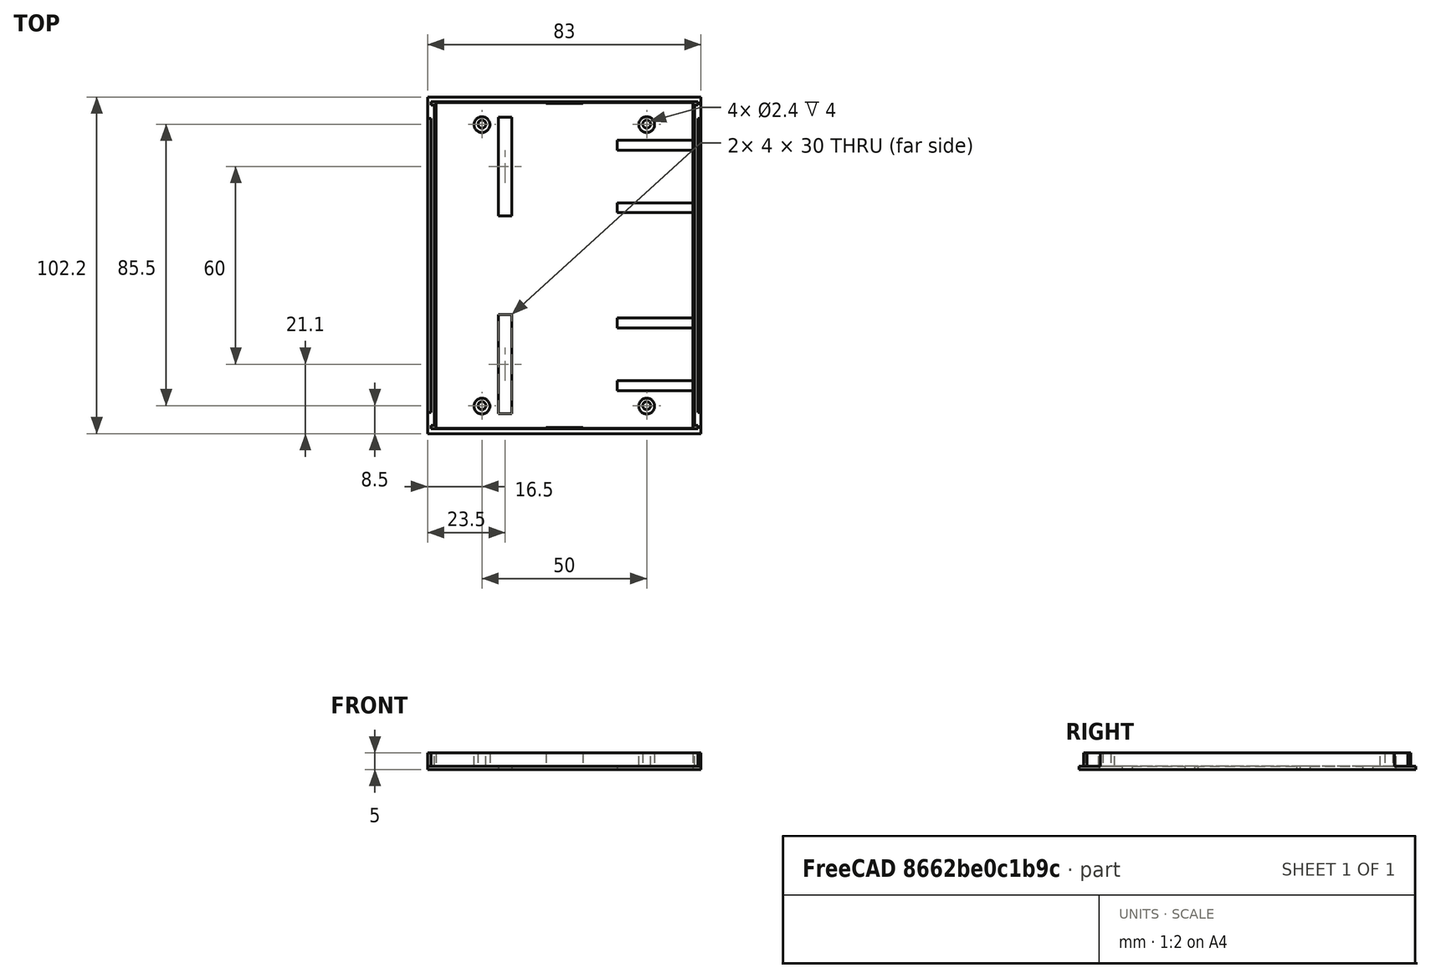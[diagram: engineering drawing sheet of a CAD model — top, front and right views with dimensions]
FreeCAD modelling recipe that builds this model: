
FCSTD DOCUMENT  (FreeCAD 1.0R39109 (Git))
Label: parte de abajo 2.0
License: All rights reserved
LicenseURL: https://en.wikipedia.org/wiki/All_rights_reserved
objects: Sketcher::SketchObject×4, PartDesign::Pad×2, PartDesign::Pocket×2, PartDesign::Body×1
note: 21 computed .brp shape members not serialized (recipe doc carries the construction recipe); baked Part::Feature solids carry a one-line shape summary decoded from their .brp

FEATURE [Sketcher::SketchObject] Sketch
  ArcFitTolerance = 1e-06
  AttachmentSupport = -> [XY_Plane]
  FullyConstrained = true
  MakeInternals = false
  MapMode = 5
  sketch-geometry (5):
    g0: LineSegment StartX=-41.5 StartY=-51.1 StartZ=0 EndX=41.5 EndY=-51.1 EndZ=0
    g1: LineSegment StartX=41.5 StartY=-51.1 StartZ=0 EndX=41.5 EndY=51.1 EndZ=0
    g2: LineSegment StartX=41.5 StartY=51.1 StartZ=0 EndX=-41.5 EndY=51.1 EndZ=0
    g3: LineSegment StartX=-41.5 StartY=51.1 StartZ=0 EndX=-41.5 EndY=-51.1 EndZ=0
    g4: GeomPoint [constr] X=0 Y=0 Z=0
  constraints (12):
    c: Coincident(g0,g1)
    c: Coincident(g1,g2)
    c: Coincident(g2,g3)
    c: Coincident(g3,g0)
    c: Horizontal(g0)
    c: Horizontal(g2)
    c: Vertical(g1)
    c: Vertical(g3)
    c: Symmetric(g2,g0,g4)
    c: Coincident(g4,g-1)
    c: DistanceX(g2,g2) = 83
    c: DistanceY(g1,g1) = 102.2
FEATURE [PartDesign::Pad] Pad
  Direction = (0,0,1)
  Length = 1
  Length2 = 10
  Profile = -> Sketch
  ReferenceAxis = -> Sketch [N_Axis]
  Refine = true
  Suppressed = false
  Type = 0
FEATURE [Sketcher::SketchObject] Sketch001
  ArcFitTolerance = 1e-06
  AttachmentSupport = -> [Pad]
  ExternalGeometry = -> [Pad]
  FullyConstrained = true
  MakeInternals = false
  MapMode = 5
  Placement = pos=(0,0,1) rot=(0,0,1;0rad)
  sketch-geometry (33):
    g0: LineSegment StartX=-39.5 StartY=-49.65 StartZ=0 EndX=39.5 EndY=-49.65 EndZ=0
    g1: LineSegment StartX=39.5 StartY=-49.65 StartZ=0 EndX=39.5 EndY=49.65 EndZ=0
    g2: LineSegment StartX=39.5 StartY=49.65 StartZ=0 EndX=-39.5 EndY=49.65 EndZ=0
    g3: LineSegment StartX=-39.5 StartY=49.65 StartZ=0 EndX=-39.5 EndY=-49.65 EndZ=0
    g4: GeomPoint [constr] X=0 Y=0 Z=0
    g5: LineSegment StartX=41.5 StartY=44.65 StartZ=0 EndX=40.5 EndY=44.65 EndZ=0
    g6: LineSegment StartX=40.5 StartY=44.65 StartZ=0 EndX=40.5 EndY=-44.65 EndZ=0
    g7: LineSegment StartX=40.5 StartY=-44.65 StartZ=0 EndX=41.5 EndY=-44.65 EndZ=0
    g8: LineSegment StartX=41.5 StartY=-44.65 StartZ=0 EndX=41.5 EndY=44.65 EndZ=0
    g9: LineSegment StartX=-41.5 StartY=44.65 StartZ=0 EndX=-41.5 EndY=-44.65 EndZ=0
    g10: LineSegment StartX=-41.5 StartY=-44.65 StartZ=0 EndX=-40.5 EndY=-44.65 EndZ=0
    g11: LineSegment StartX=-40.5 StartY=-44.65 StartZ=0 EndX=-40.5 EndY=44.65 EndZ=0
    g12: LineSegment StartX=-40.5 StartY=44.65 StartZ=0 EndX=-41.5 EndY=44.65 EndZ=0
    g13: LineSegment StartX=39.5 StartY=-49.65 StartZ=0 EndX=40.5 EndY=-49.65 EndZ=0
    g14: LineSegment StartX=40.5 StartY=-49.65 StartZ=0 EndX=40.5 EndY=-48.65 EndZ=0
    g15: LineSegment StartX=40.5 StartY=-48.65 StartZ=0 EndX=39.5 EndY=-48.65 EndZ=0
    g16: LineSegment StartX=39.5 StartY=-48.65 StartZ=0 EndX=39.5 EndY=-49.65 EndZ=0
    g17: LineSegment StartX=-39.5 StartY=-49.65 StartZ=0 EndX=-39.5 EndY=-48.65 EndZ=0
    g18: LineSegment StartX=-39.5 StartY=-48.65 StartZ=0 EndX=-40.5 EndY=-48.65 EndZ=0
    g19: LineSegment StartX=-40.5 StartY=-48.65 StartZ=0 EndX=-40.5 EndY=-49.65 EndZ=0
    g20: LineSegment StartX=-40.5 StartY=-49.65 StartZ=0 EndX=-39.5 EndY=-49.65 EndZ=0
    g21: LineSegment StartX=-39.5 StartY=49.65 StartZ=0 EndX=-40.5 EndY=49.65 EndZ=0
    g22: LineSegment StartX=-40.5 StartY=49.65 StartZ=0 EndX=-40.5 EndY=48.65 EndZ=0
    g23: LineSegment StartX=-40.5 StartY=48.65 StartZ=0 EndX=-39.5 EndY=48.65 EndZ=0
    g24: LineSegment StartX=-39.5 StartY=48.65 StartZ=0 EndX=-39.5 EndY=49.65 EndZ=0
    g25: LineSegment StartX=39.5 StartY=49.65 StartZ=0 EndX=39.5 EndY=48.65 EndZ=0
    g26: LineSegment StartX=39.5 StartY=48.65 StartZ=0 EndX=40.5 EndY=48.65 EndZ=0
    g27: LineSegment StartX=40.5 StartY=48.65 StartZ=0 EndX=40.5 EndY=49.65 EndZ=0
    g28: LineSegment StartX=40.5 StartY=49.65 StartZ=0 EndX=39.5 EndY=49.65 EndZ=0
    g29: Circle CenterX=-25 CenterY=42.9 CenterZ=0 NormalX=0 NormalY=0 NormalZ=1 AngleXU=0 Radius=1.2
    g30: Circle CenterX=25 CenterY=42.9 CenterZ=0 NormalX=0 NormalY=0 NormalZ=1 AngleXU=0 Radius=1.2
    g31: Circle CenterX=-25 CenterY=-42.6 CenterZ=0 NormalX=0 NormalY=0 NormalZ=1 AngleXU=0 Radius=1.2
    g32: Circle CenterX=25 CenterY=-42.6 CenterZ=0 NormalX=0 NormalY=0 NormalZ=1 AngleXU=0 Radius=1.2
  constraints (92):
    c: Coincident(g0,g1)
    c: Coincident(g1,g2)
    c: Coincident(g2,g3)
    c: Coincident(g3,g0)
    c: Horizontal(g0)
    c: Horizontal(g2)
    c: Vertical(g1)
    c: Vertical(g3)
    c: Symmetric(g2,g0,g4)
    c: Coincident(g4,g-1)
    c: DistanceY(g1,g1) = 99.3
    c: DistanceX(g2,g2) = 79
    c: Coincident(g5,g6)
    c: Coincident(g6,g7)
    c: Coincident(g7,g8)
    c: Coincident(g8,g5)
    c: Horizontal(g5)
    c: Horizontal(g7)
    c: Vertical(g6)
    c: Vertical(g8)
    c: PointOnObject(g5,g-6)
    c: DistanceX(g5,g5) = 1
    c: DistanceY(g8,g8) = 89.3
    c: DistanceY(g0,g7) = 5
    c: Coincident(g9,g10)
    c: Coincident(g10,g11)
    c: Coincident(g11,g12)
    c: Coincident(g12,g9)
    c: Vertical(g9)
    c: Vertical(g11)
    c: Horizontal(g10)
    c: Horizontal(g12)
    c: PointOnObject(g9,g-4)
    c: DistanceX(g12,g12) = 1
    c: DistanceY(g9,g9) = 89.3
    c: Distance(g0,g10) = 5
    c: Coincident(g13,g14)
    c: Coincident(g14,g15)
    c: Coincident(g15,g16)
    c: Coincident(g16,g13)
    c: Horizontal(g13)
    c: Horizontal(g15)
    c: Vertical(g14)
    c: Vertical(g16)
    c: Coincident(g13,g0)
    c: DistanceX(g15,g15) = 1
    c: DistanceY(g14,g14) = 1
    c: Coincident(g17,g18)
    c: Coincident(g18,g19)
    c: Coincident(g19,g20)
    c: Coincident(g20,g17)
    c: Vertical(g17)
    c: Vertical(g19)
    c: Horizontal(g18)
    c: Horizontal(g20)
    c: Coincident(g17,g0)
    c: DistanceX(g18,g18) = 1
    c: DistanceY(g19,g19) = 1
    c: Coincident(g21,g22)
    c: Coincident(g22,g23)
    c: Coincident(g23,g24)
    c: Coincident(g24,g21)
    c: Horizontal(g21)
    c: Horizontal(g23)
    c: Vertical(g22)
    c: Vertical(g24)
    c: Coincident(g21,g2)
    c: DistanceY(g22,g22) = 1
    c: DistanceX(g23,g23) = 1
    c: Coincident(g25,g26)
    c: Coincident(g26,g27)
    c: Coincident(g27,g28)
    c: Coincident(g28,g25)
    c: Vertical(g25)
    c: Vertical(g27)
    c: Horizontal(g26)
    c: Horizontal(g28)
    c: Coincident(g25,g1)
    c: DistanceX(g26,g26) = 1
    c: DistanceY(g27,g27) = 1
    c: Diameter(g29) = 2.4
    c: Distance(g29,g2) = 6.75
    c: Diameter(g30) = 2.4
    c: Distance(g30,g2) = 6.75
    c: DistanceX(g29,g30) = 50
    c: Distance(g29,g3) = 14.5
    c: Diameter(g31) = 2.4
    c: Distance(g29,g31) = 85.5
    c: Distance(g31,g3) = 14.5
    c: DistanceX(g31,g32) = 50
    c: Diameter(g32) = 2.4
    c: DistanceY(g32,g30) = 85.5
FEATURE [PartDesign::Pad] Pad001
  BaseFeature = -> Pad
  Direction = (0,0,1)
  Length = 4
  Length2 = 10
  Profile = -> Sketch001
  ReferenceAxis = -> Sketch001 [N_Axis]
  Refine = true
  Suppressed = false
  Type = 0
FEATURE [Sketcher::SketchObject] Sketch002
  ArcFitTolerance = 1e-06
  AttachmentSupport = -> [Pad001]
  ExternalGeometry = -> [Pad001]
  FullyConstrained = true
  MakeInternals = false
  MapMode = 5
  Placement = pos=(0,0,5) rot=(0,0,1;0rad)
  sketch-geometry (17):
    g0: LineSegment StartX=-39 StartY=-49.5 StartZ=0 EndX=39 EndY=-49.5 EndZ=0
    g1: LineSegment StartX=39 StartY=-49.5 StartZ=0 EndX=39 EndY=49.5 EndZ=0
    g2: LineSegment StartX=39 StartY=49.5 StartZ=0 EndX=-39 EndY=49.5 EndZ=0
    g3: LineSegment StartX=-39 StartY=49.5 StartZ=0 EndX=-39 EndY=-49.5 EndZ=0
    g4: GeomPoint [constr] X=0 Y=0 Z=0
    g5: LineSegment StartX=-5.6 StartY=-49.5 StartZ=0 EndX=5.6 EndY=-49.5 EndZ=0
    g6: LineSegment StartX=5.6 StartY=-49.5 StartZ=0 EndX=5.6 EndY=-49.2 EndZ=0
    g7: LineSegment StartX=5.6 StartY=-49.2 StartZ=0 EndX=-5.6 EndY=-49.2 EndZ=0
    g8: LineSegment StartX=-5.6 StartY=-49.2 StartZ=0 EndX=-5.6 EndY=-49.5 EndZ=0
    g9: Circle CenterX=-25 CenterY=-42.75 CenterZ=0 NormalX=0 NormalY=0 NormalZ=1 AngleXU=0 Radius=2.4
    g10: Circle CenterX=-25 CenterY=42.75 CenterZ=0 NormalX=0 NormalY=0 NormalZ=1 AngleXU=0 Radius=2.4
    g11: Circle CenterX=25 CenterY=42.75 CenterZ=0 NormalX=0 NormalY=0 NormalZ=1 AngleXU=0 Radius=2.4
    g12: Circle CenterX=25 CenterY=-42.75 CenterZ=0 NormalX=0 NormalY=0 NormalZ=1 AngleXU=0 Radius=2.4
    g13: LineSegment StartX=-5.6 StartY=49.5 StartZ=0 EndX=-5.6 EndY=49.2 EndZ=0
    g14: LineSegment StartX=-5.6 StartY=49.2 StartZ=0 EndX=5.6 EndY=49.2 EndZ=0
    g15: LineSegment StartX=5.6 StartY=49.2 StartZ=0 EndX=5.6 EndY=49.5 EndZ=0
    g16: LineSegment StartX=5.6 StartY=49.5 StartZ=0 EndX=-5.6 EndY=49.5 EndZ=0
  constraints (48):
    c: Coincident(g0,g1)
    c: Coincident(g1,g2)
    c: Coincident(g2,g3)
    c: Coincident(g3,g0)
    c: Horizontal(g0)
    c: Horizontal(g2)
    c: Vertical(g1)
    c: Vertical(g3)
    c: Symmetric(g2,g0,g4)
    c: Coincident(g4,g-1)
    c: DistanceX(g2,g2) = 78
    c: DistanceY(g1,g1) = 99
    c: Coincident(g5,g6)
    c: Coincident(g6,g7)
    c: Coincident(g7,g8)
    c: Coincident(g8,g5)
    c: Horizontal(g5)
    c: Horizontal(g7)
    c: Vertical(g6)
    c: Vertical(g8)
    c: PointOnObject(g5,g0)
    c: DistanceX(g7,g7) = 11.2
    c: DistanceY(g6,g6) = 0.3
    c: Distance(g0,g8) = 33.4
    c: Diameter(g9) = 4.8
    c: Distance(g9,g3) = 14
    c: Diameter(g10) = 4.8
    c: Distance(g10,g2) = 6.75
    c: Distance(g10,g3) = 14
    c: DistanceY(g9,g10) = 85.5
    c: Diameter(g11) = 4.8
    c: Distance(g11,g2) = 6.75
    c: Distance(g10,g11) = 50
    c: Diameter(g12) = 4.8
    c: DistanceX(g9,g12) = 50
    c: DistanceY(g12,g11) = 85.5
    c: Coincident(g13,g14)
    c: Coincident(g14,g15)
    c: Coincident(g15,g16)
    c: Coincident(g16,g13)
    c: Vertical(g13)
    c: Vertical(g15)
    c: Horizontal(g14)
    c: Horizontal(g16)
    c: PointOnObject(g13,g2)
    c: DistanceY(g13,g13) = 0.3
    c: DistanceX(g14,g14) = 11.2
    c: Distance(g1,g15) = 33.4
FEATURE [PartDesign::Pocket] Pocket
  BaseFeature = -> Pad001
  Direction = (0,0,-1)
  Length = 4
  Length2 = 5
  Profile = -> Sketch002
  ReferenceAxis = -> Sketch002 [N_Axis]
  Refine = true
  Suppressed = false
  Type = 0
FEATURE [Sketcher::SketchObject] Sketch003
  ArcFitTolerance = 1e-06
  AttachmentSupport = -> [Pocket]
  ExternalGeometry = -> [Pocket]
  FullyConstrained = true
  MakeInternals = false
  MapMode = 5
  Placement = pos=(0,0,1) rot=(0,0,1;0rad)
  sketch-geometry (24):
    g0: LineSegment StartX=-20 StartY=-15 StartZ=0 EndX=-20 EndY=-45 EndZ=0
    g1: LineSegment StartX=-20 StartY=-45 StartZ=0 EndX=-16 EndY=-45 EndZ=0
    g2: LineSegment StartX=-16 StartY=-45 StartZ=0 EndX=-16 EndY=-15 EndZ=0
    g3: LineSegment StartX=-16 StartY=-15 StartZ=0 EndX=-20 EndY=-15 EndZ=0
    g4: LineSegment StartX=-20 StartY=45 StartZ=0 EndX=-20 EndY=15 EndZ=0
    g5: LineSegment StartX=-20 StartY=15 StartZ=0 EndX=-16 EndY=15 EndZ=0
    g6: LineSegment StartX=-16 StartY=15 StartZ=0 EndX=-16 EndY=45 EndZ=0
    g7: LineSegment StartX=-16 StartY=45 StartZ=0 EndX=-20 EndY=45 EndZ=0
    g8: LineSegment StartX=16 StartY=38 StartZ=0 EndX=16 EndY=35 EndZ=0
    g9: LineSegment StartX=16 StartY=35 StartZ=0 EndX=39 EndY=35 EndZ=0
    g10: LineSegment StartX=39 StartY=35 StartZ=0 EndX=39 EndY=38 EndZ=0
    g11: LineSegment StartX=39 StartY=38 StartZ=0 EndX=16 EndY=38 EndZ=0
    g12: LineSegment StartX=16 StartY=19 StartZ=0 EndX=16 EndY=16 EndZ=0
    g13: LineSegment StartX=16 StartY=16 StartZ=0 EndX=39 EndY=16 EndZ=0
    g14: LineSegment StartX=39 StartY=16 StartZ=0 EndX=39 EndY=19 EndZ=0
    g15: LineSegment StartX=39 StartY=19 StartZ=0 EndX=16 EndY=19 EndZ=0
    g16: LineSegment StartX=16 StartY=-16 StartZ=0 EndX=16 EndY=-19 EndZ=0
    g17: LineSegment StartX=16 StartY=-19 StartZ=0 EndX=39 EndY=-19 EndZ=0
    g18: LineSegment StartX=39 StartY=-19 StartZ=0 EndX=39 EndY=-16 EndZ=0
    g19: LineSegment StartX=39 StartY=-16 StartZ=0 EndX=16 EndY=-16 EndZ=0
    g20: LineSegment StartX=16 StartY=-35 StartZ=0 EndX=16 EndY=-38 EndZ=0
    g21: LineSegment StartX=16 StartY=-38 StartZ=0 EndX=39 EndY=-38 EndZ=0
    g22: LineSegment StartX=39 StartY=-38 StartZ=0 EndX=39 EndY=-35 EndZ=0
    g23: LineSegment StartX=39 StartY=-35 StartZ=0 EndX=16 EndY=-35 EndZ=0
  constraints (72):
    c: Coincident(g0,g1)
    c: Coincident(g1,g2)
    c: Coincident(g2,g3)
    c: Coincident(g3,g0)
    c: Vertical(g0)
    c: Vertical(g2)
    c: Horizontal(g1)
    c: Horizontal(g3)
    c: Coincident(g4,g5)
    c: Coincident(g5,g6)
    c: Coincident(g6,g7)
    c: Coincident(g7,g4)
    c: Vertical(g4)
    c: Vertical(g6)
    c: Horizontal(g5)
    c: Horizontal(g7)
    c: DistanceY(g6,g6) = 30
    c: DistanceX(g5,g5) = 4
    c: DistanceX(g3,g3) = 4
    c: DistanceY(g2,g2) = 30
    c: Distance(g-1,g3) = 15
    c: Distance(g-2,g2) = 16
    c: Distance(g-2,g6) = 16
    c: Distance(g-1,g5) = 15
    c: Coincident(g8,g9)
    c: Coincident(g9,g10)
    c: Coincident(g10,g11)
    c: Coincident(g11,g8)
    c: Vertical(g8)
    c: Vertical(g10)
    c: Horizontal(g9)
    c: Horizontal(g11)
    c: Coincident(g12,g13)
    c: Coincident(g13,g14)
    c: Coincident(g14,g15)
    c: Coincident(g15,g12)
    c: Vertical(g12)
    c: Vertical(g14)
    c: Horizontal(g13)
    c: Horizontal(g15)
    c: Coincident(g16,g17)
    c: Coincident(g17,g18)
    c: Coincident(g18,g19)
    c: Coincident(g19,g16)
    c: Vertical(g16)
    c: Vertical(g18)
    c: Horizontal(g17)
    c: Horizontal(g19)
    c: DistanceY(g16,g16) = 3
    c: DistanceY(g12,g12) = 3
    c: DistanceX(g15,g15) = 23
    c: DistanceX(g19,g19) = 23
    c: Distance(g-2,g16) = 16
    c: Distance(g-2,g12) = 16
    c: Distance(g-1,g19) = 16
    c: Distance(g-1,g13) = 16
    c: Coincident(g20,g21)
    c: Coincident(g21,g22)
    c: Coincident(g22,g23)
    c: Coincident(g23,g20)
    c: Vertical(g20)
    c: Vertical(g22)
    c: Horizontal(g21)
    c: Horizontal(g23)
    c: Distance(g-2,g20) = 16
    c: DistanceY(g20,g20) = 3
    c: DistanceX(g21,g21) = 23
    c: Distance(g17,g23) = 16
    c: DistanceY(g8,g8) = 3
    c: DistanceX(g11,g11) = 23
    c: Distance(g-2,g8) = 16
    c: Distance(g15,g9) = 16
FEATURE [PartDesign::Pocket] Pocket001
  BaseFeature = -> Pocket
  Direction = (0,0,-1)
  Length = 2
  Length2 = 5
  Profile = -> Sketch003
  ReferenceAxis = -> Sketch003 [N_Axis]
  Refine = true
  Suppressed = false
  Type = 0
FEATURE [PartDesign::Body] Body
  AllowCompound = false
  Group = -> [Sketch,Pad,Sketch001,Pad001,Sketch002,Pocket,Sketch003,Pocket001]
  Origin = -> Origin
  Tip = -> Pocket001
